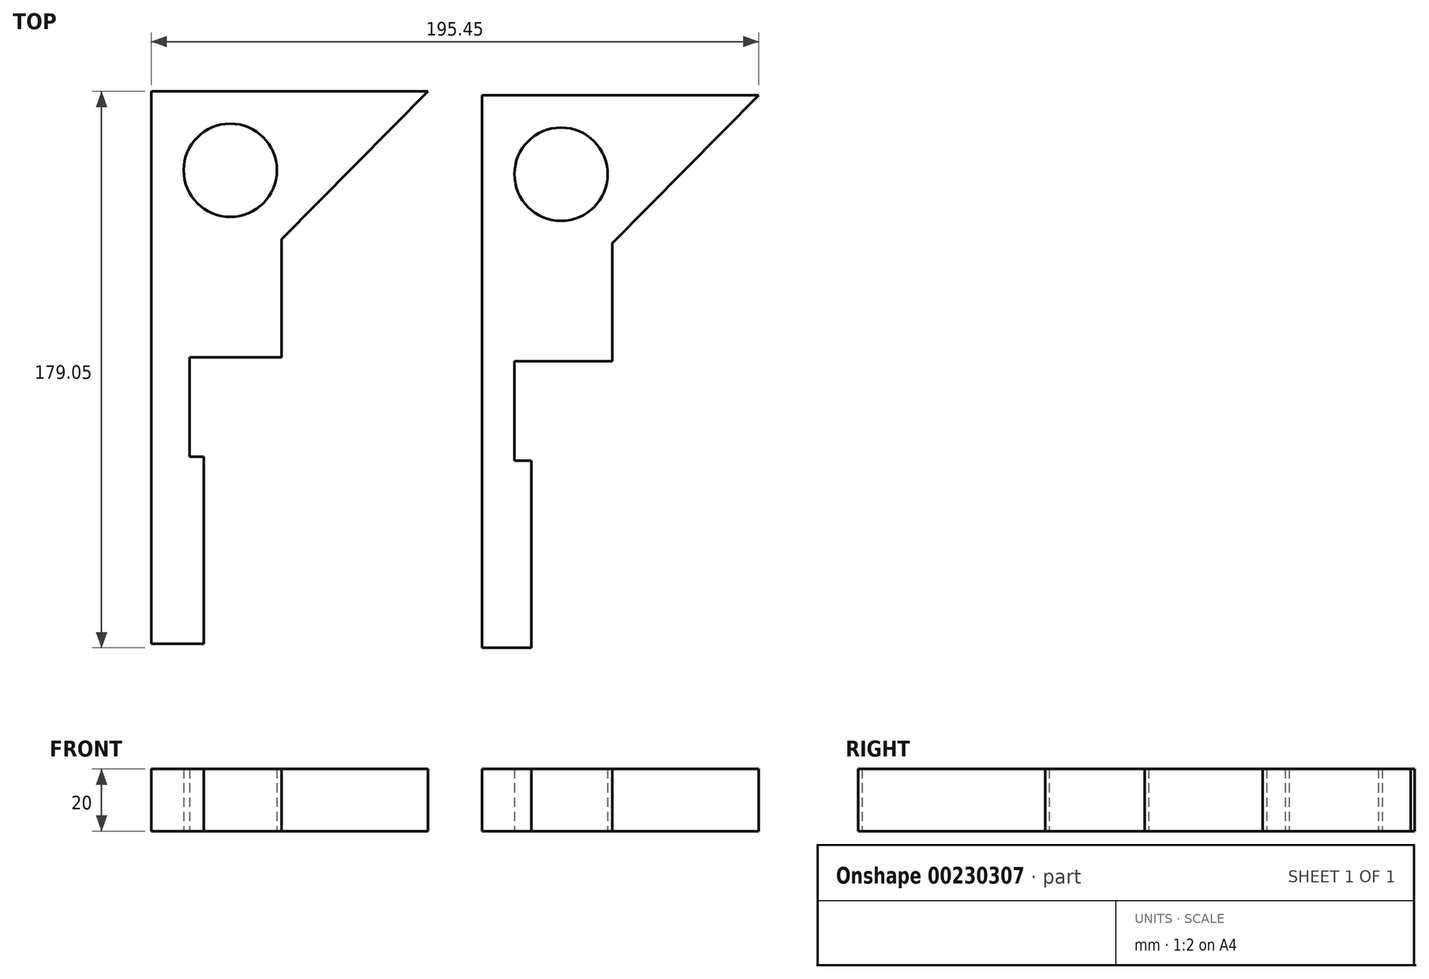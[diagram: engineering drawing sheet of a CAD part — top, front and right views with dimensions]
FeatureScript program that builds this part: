
annotation { "Feature Type Name" : "Feature", "Feature Type Description" : "" }
export const myFeature = defineFeature(function(context is Context, id is Id, definition is map)
    precondition{}
    {
        {
            var Q0;
            Q0=qCreatedBy(makeId("Top.planeOp"),FACE);
            var sketch = newSketch(context, id + "F0", { "sketchPlane" : qUnion([Q0])});
            skLineSegment(sketch, "E0", {"start": v(-46.93, 106.64) * mm, "end": v(42.07, 106.64) * mm});
            skLineSegment(sketch, "E1", {"start": v(42.07, 106.64) * mm, "end": v(-5.06, 59.02) * mm});
            skLineSegment(sketch, "E2", {"start": v(-5.06, 59.02) * mm, "end": v(-5.06, 21.02) * mm});
            skLineSegment(sketch, "E3", {"start": v(-5.06, 21.02) * mm, "end": v(-34.56, 21.02) * mm});
            skLineSegment(sketch, "E4", {"start": v(-34.56, 21.02) * mm, "end": v(-34.56, -10.98) * mm});
            skLineSegment(sketch, "E5", {"start": v(-34.56, -10.98) * mm, "end": v(-30.06, -10.98) * mm});
            skLineSegment(sketch, "E6", {"start": v(-30.06, -10.98) * mm, "end": v(-30.06, -48.98) * mm});
            skLineSegment(sketch, "E7", {"start": v(-30.06, -48.98) * mm, "end": v(-30.06, -48.98) * mm});
            skLineSegment(sketch, "E8", {"start": v(-30.06, -48.98) * mm, "end": v(-30.06, -71.16) * mm});
            skLineSegment(sketch, "E9", {"start": v(-30.06, -71.16) * mm, "end": v(-46.93, -71.16) * mm});
            skLineSegment(sketch, "E10", {"start": v(-46.93, -71.16) * mm, "end": v(-46.93, 106.64) * mm});
            skCircle(sketch, "E11", {"center": v(-21.53, 81.24) * mm, "radius": 15 * mm});
            skSolve(sketch);
        }
        {
            var Q0;
            Q0=makeQuery(id+"F0.imprint","IMPRINT",FACE,{"disambiguationData":[TD([[makeQuery(id+"F0.imprint","IMPRINT",EDGE,{"derivedFrom":sQuery(id+"F0.wireOp",EDGE,"E0")}),-1.0]])]});
            extrude(context, id + "F1", {"entities" : qUnion([Q0]), "depth" : 20 * mm});
        }
        {
            var Q0;
            Q0=qCreatedBy(makeId("Top.planeOp"),FACE);
            var sketch = newSketch(context, id + "F2", { "sketchPlane" : qUnion([Q0])});
            skLineSegment(sketch, "E12", {"start": v(59.52, 105.39) * mm, "end": v(148.52, 105.39) * mm});
            skLineSegment(sketch, "E13", {"start": v(148.52, 105.39) * mm, "end": v(101.39, 57.77) * mm});
            skLineSegment(sketch, "E14", {"start": v(101.39, 57.77) * mm, "end": v(101.39, 19.77) * mm});
            skLineSegment(sketch, "E15", {"start": v(101.39, 19.77) * mm, "end": v(69.89, 19.77) * mm});
            skLineSegment(sketch, "E16", {"start": v(69.89, 19.77) * mm, "end": v(69.89, -12.23) * mm});
            skLineSegment(sketch, "E17", {"start": v(69.89, -12.23) * mm, "end": v(75.39, -12.23) * mm});
            skLineSegment(sketch, "E18", {"start": v(75.39, -12.23) * mm, "end": v(75.39, -50.23) * mm});
            skLineSegment(sketch, "E19", {"start": v(75.39, -50.23) * mm, "end": v(75.39, -50.23) * mm});
            skLineSegment(sketch, "E20", {"start": v(75.39, -50.23) * mm, "end": v(75.39, -72.41) * mm});
            skLineSegment(sketch, "E21", {"start": v(75.39, -72.41) * mm, "end": v(59.52, -72.41) * mm});
            skLineSegment(sketch, "E22", {"start": v(59.52, -72.41) * mm, "end": v(59.52, 105.39) * mm});
            skCircle(sketch, "E23", {"center": v(84.92, 79.99) * mm, "radius": 15 * mm});
            skLineSegment(sketch, "E24.bottom", {"start": v(59.52, 105.39) * mm, "end": v(59.52, 105.39) * mm});
            skSolve(sketch);
        }
        {
            var Q0;
            Q0 = qSketchRegion(id + "F2", true);
            extrude(context, id + "F3", {"entities" : qUnion([Q0]), "depth" : 20 * mm});
        }
    });
